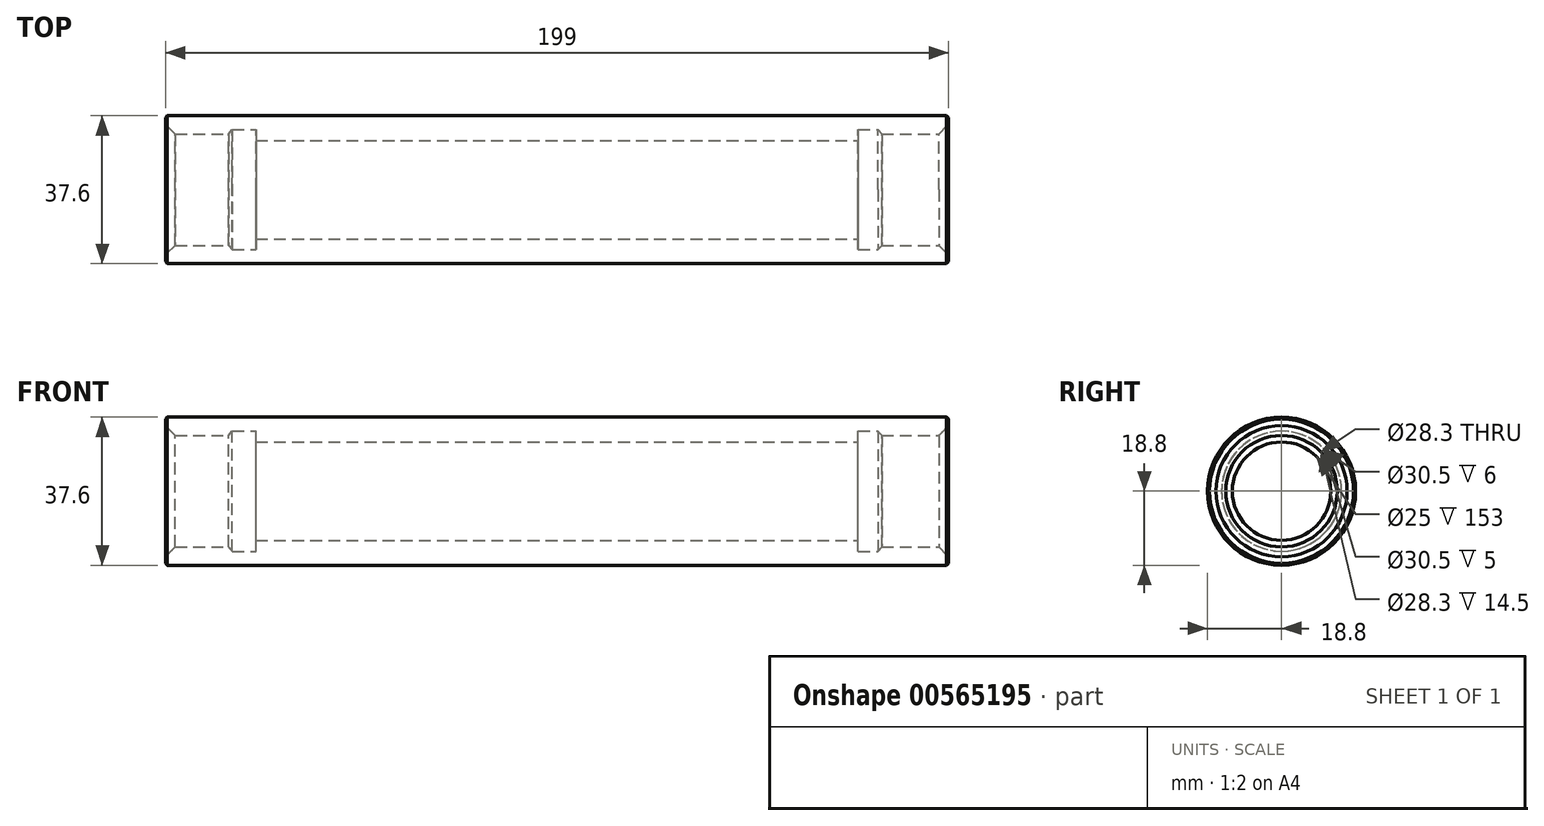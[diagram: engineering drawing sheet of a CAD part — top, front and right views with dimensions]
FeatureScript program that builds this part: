
annotation { "Feature Type Name" : "Feature", "Feature Type Description" : "" }
export const myFeature = defineFeature(function(context is Context, id is Id, definition is map)
    precondition{}
    {
        {
            var Q0;
            Q0=qCreatedBy(makeId("Front.planeOp"),FACE);
            var sketch = newSketch(context, id + "F0", { "sketchPlane" : qUnion([Q0])});
            skLineSegment(sketch, "E0", {"start": v(0, 0) * mm, "end": v(0, 18.8) * mm});
            skLineSegment(sketch, "E1", {"start": v(0, 18.8) * mm, "end": v(199, 18.8) * mm});
            skLineSegment(sketch, "E2", {"start": v(199, 18.8) * mm, "end": v(199, 0) * mm});
            skLineSegment(sketch, "E3", {"start": v(199, 0) * mm, "end": v(0, 0) * mm, "construction": true});
            skLineSegment(sketch, "E4", {"start": v(0, 14.15) * mm, "end": v(17, 14.15) * mm});
            skLineSegment(sketch, "E5", {"start": v(17, 14.15) * mm, "end": v(17, 15.25) * mm});
            skLineSegment(sketch, "E6", {"start": v(17, 15.25) * mm, "end": v(23, 15.25) * mm});
            skLineSegment(sketch, "E7", {"start": v(23, 15.25) * mm, "end": v(23, 12.5) * mm});
            skLineSegment(sketch, "E8", {"start": v(23, 12.5) * mm, "end": v(176, 12.5) * mm});
            skLineSegment(sketch, "E9", {"start": v(176, 12.5) * mm, "end": v(176, 15.25) * mm});
            skLineSegment(sketch, "E10", {"start": v(176, 15.25) * mm, "end": v(182, 15.25) * mm});
            skLineSegment(sketch, "E11", {"start": v(182, 15.25) * mm, "end": v(182, 14.15) * mm});
            skLineSegment(sketch, "E12", {"start": v(182, 14.15) * mm, "end": v(199, 14.15) * mm});
            skLineSegment(sketch, "E13", {"start": v(99.5, 18.8) * mm, "end": v(99.5, 12.5) * mm});
            skSolve(sketch);
        }
        {
            var Q0;
            {var subQ0=sQuery(id+"F0.wireOp",EDGE,"E1");Q0=makeQuery(id+"F0.imprint","IMPRINT",FACE,{"disambiguationData":[TD([[makeQuery(id+"F0.imprint","IMPRINT",EDGE,{"derivedFrom":subQ0}),-1.0]])]});}
            var Q1;
            Q1=sQuery(id+"F0.wireOp",EDGE,"E3");
            revolve(context, id + "F1", {"entities" : qUnion([Q0]), "axis" : qUnion([Q1]), "revolveType" : RevolveType.FULL, "surfaceOperationType" : NewSurfaceOperationType.NEW});
        }
        {
            var Q0;
            Q0=makeQuery(id+"F1.opRevolve","SWEPT_EDGE",EDGE,{"disambiguationData":[OSD([sQuery(id+"F0.wireOp",EDGE,"E1"),sQuery(id+"F0.wireOp",EDGE,"E2")])]});
            var Q1;
            Q1=makeQuery(id+"F1.opRevolve","SWEPT_EDGE",EDGE,{"disambiguationData":[OSD([sQuery(id+"F0.wireOp",EDGE,"E0"),sQuery(id+"F0.wireOp",EDGE,"E1")])]});
            chamfer(context, id + "F2", {"entities" : qUnion([Q0, Q1]), "width" : 0.5 * mm, "tangentPropagation" : true});
        }
        {
            var Q0;
            Q0=makeQuery(id+"F1.opRevolve","SWEPT_EDGE",EDGE,{"disambiguationData":[OSD([sQuery(id+"F0.wireOp",EDGE,"E0"),sQuery(id+"F0.wireOp",EDGE,"E4")])]});
            chamfer(context, id + "F3", {"entities" : qUnion([Q0]), "width" : 2.5 * mm, "tangentPropagation" : true});
        }
        {
            var Q0;
            Q0=makeQuery(id+"F1.opRevolve","SWEPT_EDGE",EDGE,{"disambiguationData":[OSD([sQuery(id+"F0.wireOp",EDGE,"E2"),sQuery(id+"F0.wireOp",EDGE,"E12")])]});
            chamfer(context, id + "F4", {"entities" : qUnion([Q0]), "width" : 2.5 * mm, "tangentPropagation" : true});
        }
        {
            var Q0;
            Q0=makeQuery(id+"F1.opRevolve","SWEPT_EDGE",EDGE,{"disambiguationData":[OSD([sQuery(id+"F0.wireOp",EDGE,"E4"),sQuery(id+"F0.wireOp",EDGE,"E5")])]});
            chamfer(context, id + "F5", {"entities" : qUnion([Q0]), "chamferType" : ChamferType.TWO_OFFSETS, "width1" : 1 * mm, "oppositeDirection" : false, "width2" : 1.1 * mm, "tangentPropagation" : true});
        }
        {
            var Q0;
            Q0=makeQuery(id+"F1.opRevolve","SWEPT_EDGE",EDGE,{"disambiguationData":[OSD([sQuery(id+"F0.wireOp",EDGE,"E10"),sQuery(id+"F0.wireOp",EDGE,"E11")])]});
            chamfer(context, id + "F6", {"entities" : qUnion([Q0]), "chamferType" : ChamferType.TWO_OFFSETS, "width1" : 1 * mm, "oppositeDirection" : false, "width2" : 1.06 * mm, "tangentPropagation" : true});
        }
    });
